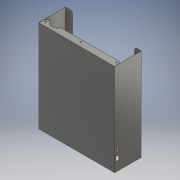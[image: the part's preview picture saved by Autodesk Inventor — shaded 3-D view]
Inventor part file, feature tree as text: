
AUTODESK INVENTOR PART (.ipt)
format: ipt  version: 2017 (Build 210142000, 142)  size: 402,944 bytes
history: native  units: mm
features: other x15, sheet_metal_op x10, sketch x9, reference x5, hole x2, chamfer x1, projected_geometry x1
ambient origin geometry x8: Origin, YZ Plane, XZ Plane, XY Plane, X Axis, Y Axis, Z Axis, Center Point
bodies: Solid1 (feature_tree)
feature tree (43):
  other  "Blocks"
  sheet_metal_op  "Face1"
  sheet_metal_op  "Flange1"
  sheet_metal_op  "Flange5"
  sheet_metal_op  "Flange6"
  chamfer  "Corner Round1"
  hole  "Hole1"  [1 undecoded]
  hole  "Hole2"  [1 undecoded]
  other  "A-Side Definition"
  sketch  "Sketch1"  dims[d0=280.0mm d1=340.0mm]
  other  "Plate1"
  sketch  "Sketch2"  dims[d2=0.5mm d3=0.5mm]
  other  "Plate2"
  sheet_metal_op  "Bend1"
  sheet_metal_op  "Corner1"
  sketch  "Sketch6"  dims[d4=0.25mm]
  other  "Plate6"
  sheet_metal_op  "Bend5"
  sheet_metal_op  "Corner5"
  sketch  "Sketch7"  dims[d5=1.0mm]
  other  "Plate7"
  sheet_metal_op  "Bend6"
  sheet_metal_op  "Corner6"
  sketch  "Sketch8"  dims[d6=0.5mm]
  sketch  "Sketch9"  dims[d7=100.0mm d8=90.0deg d9=0.5mm]
  other  "lOGO"
  projected_geometry  "Projected Loop1"
  sketch  "Sketch10"  dims[d10=2.0mm]
  sketch  "Sketch11"  dims[d11=0.5mm]
  reference  "Reference1"
  sketch  "Sketch12"  dims[d12=0.5mm d43=0.5mm d44=0.25mm d45=1.0mm d46=0.5mm d47=25.0mm d48=90.0deg d49=0.5mm d50=2.0mm d51=0.5mm d52=0.5mm d53=0.5mm d54=0.25mm d55=1.0mm d56=0.5mm d57=25.0mm d58=90.0deg d59=0.5mm d60=2.0mm d61=0.5mm d62=0.5mm d63=8.0mm d64=5.15mm d65=6.0mm d66=4.0mm d67=2.0mm d68=90.0deg d69=0.5mm d70=20.594885mm d71=9.0mm d72=14.0mm d73=45.0deg d74=4.0mm d75=4.0mm d76=7.0mm d77=35.0mm d78=9.0mm d80=0.5mm d81=0.0mm d82=7.0mm d84=20.0mm d85=50.0mm d86=108.0mm d87=64.8mm d88=133.5mm d90=84.0mm d91=12.69mm d92=11.45mm d94=3.15mm d95=3.15mm d96=3.15mm d97=3.15mm d98=77.6mm d99=127.1mm d100=1.0mm d101=5.15mm d102=6.0mm d103=4.0mm d104=2.0mm d105=90.0deg d106=0.5mm d107=20.594885mm d108=10.0mm d112=40.0mm d113=0.5mm d114=0.0mm d115=0.5mm d116=0.5mm d117=12.0mm d118=5.0mm d119=0.3mm d120=0.0mm d121=0.5mm d122=0.0mm]
  reference  "Reference2"
  reference  "Reference3"
  reference  "Reference4"
  reference  "Reference5"
  other  "Cut1"
  other  "Cut2"
  other  "Cut3"
  parser-record x1  (decoder bookkeeping rows leaked as tree rows — omitted from the tree; the rows remain in map.json)
  other  "Espectometro.iam"
  other  "CorpoSplitter:2"
  other  "MB1137:1"
  other  "Definition1"
note: 2 required parameter values undecoded (feature->parameter linkage not recoverable at this tier; creation-order binding heuristic only, values carry confidence <= 0.55)
note: 1 file-system path scrubbed to <path> (originals preserved in map.json)
